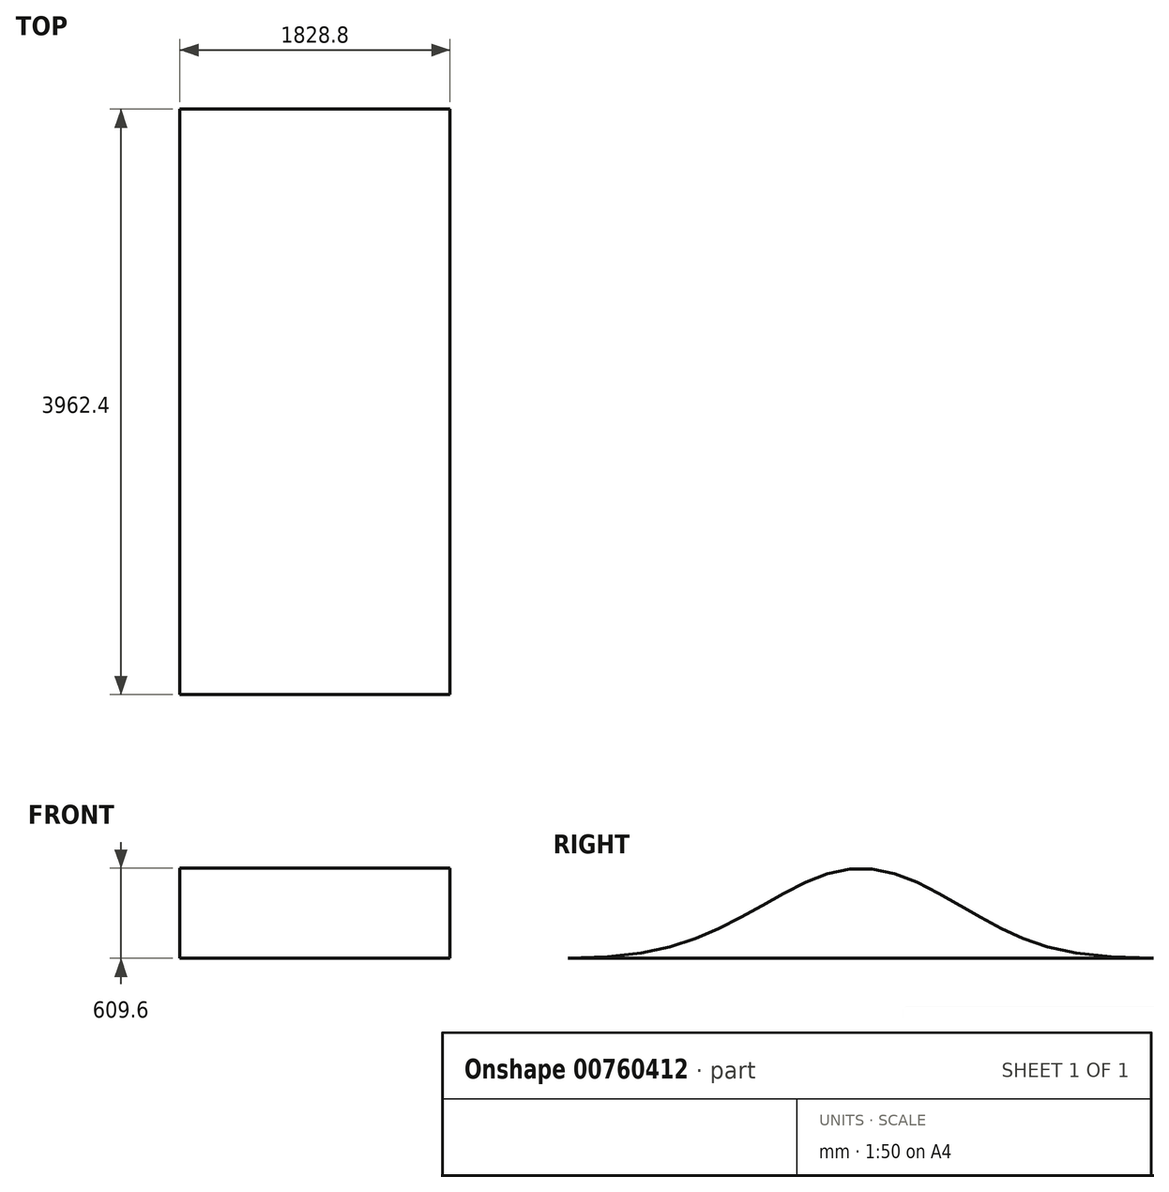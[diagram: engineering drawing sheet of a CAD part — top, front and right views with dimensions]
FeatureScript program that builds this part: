
annotation { "Feature Type Name" : "Feature", "Feature Type Description" : "" }
export const myFeature = defineFeature(function(context is Context, id is Id, definition is map)
    precondition{}
    {
        {
            var Q0;
            Q0=qCreatedBy(makeId("Right.planeOp"),FACE);
            var sketch = newSketch(context, id + "F0", { "sketchPlane" : qUnion([Q0])});
            skLineSegment(sketch, "E0", {"start": v(-289.64, -304.8) * mm, "end": v(-4252.04, -304.8) * mm});
            skFitSpline(sketch, "E1", {"points": [v(-4252.04, -304.8) * mm, v(-3032.84, 0) * mm, v(-2270.84, 304.8) * mm, v(-1508.84, 0) * mm, v(-289.64, -304.8) * mm], "startDerivative": vector(6590.87, 0) * mm, "endDerivative": vector(7300.45, 0) * mm});
            skSolve(sketch);
        }
        {
            var Q0;
            Q0 = qSketchRegion(id + "F0", true);
            extrude(context, id + "F1", {"entities" : qUnion([Q0]), "depth" : 1828.8 * mm, "offsetDistance" : 30.48 * mm});
        }
    });
